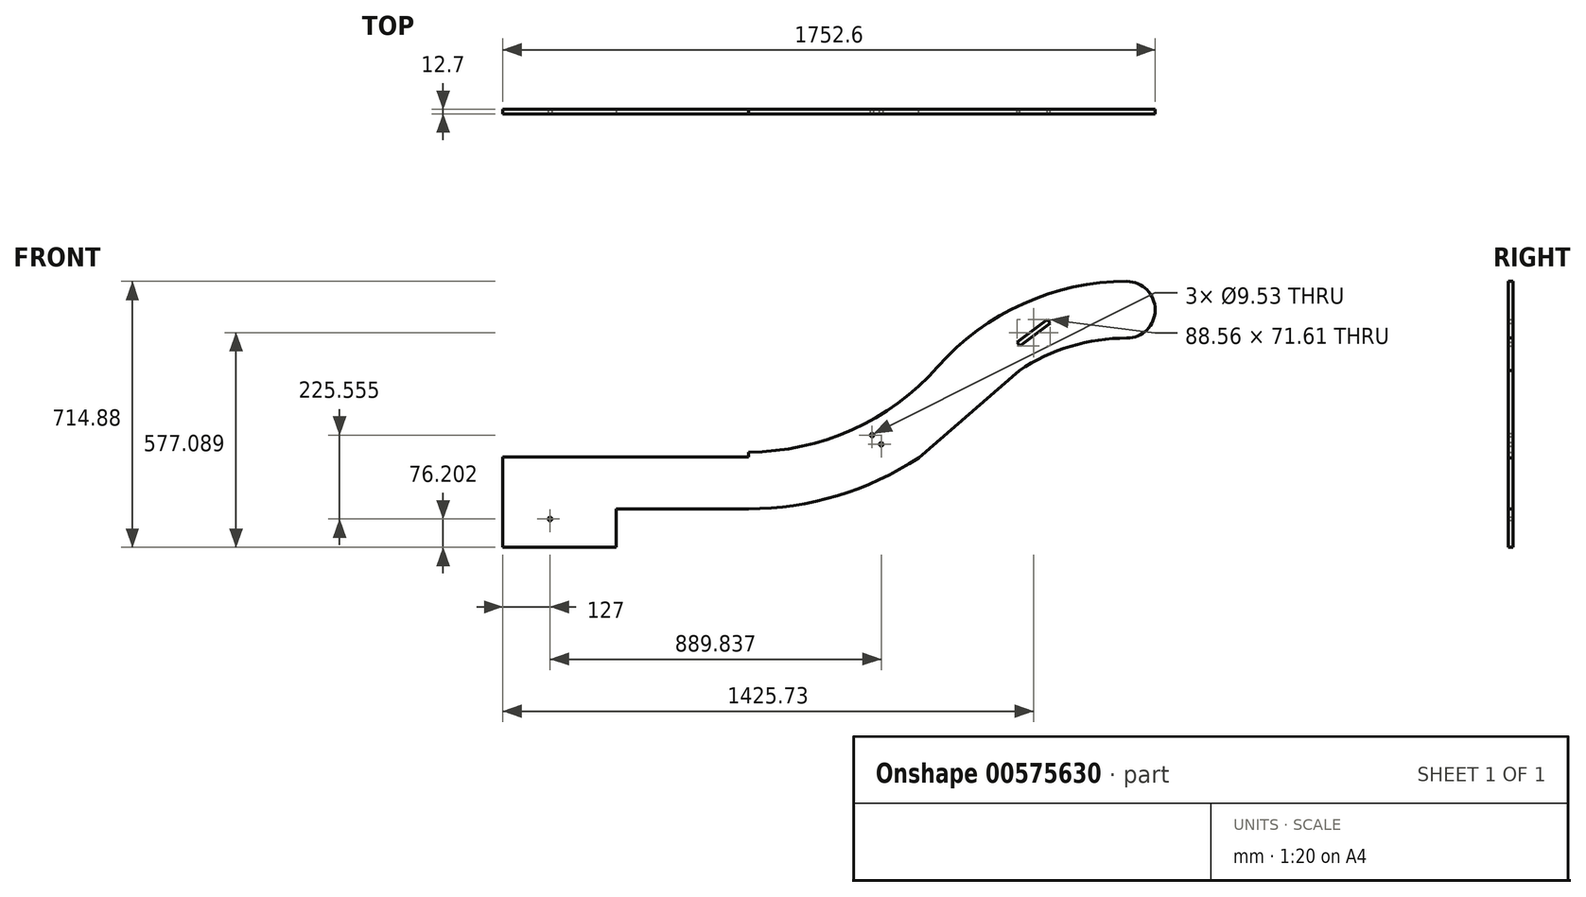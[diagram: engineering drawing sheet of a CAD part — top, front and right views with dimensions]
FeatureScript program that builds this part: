
annotation { "Feature Type Name" : "Feature", "Feature Type Description" : "" }
export const myFeature = defineFeature(function(context is Context, id is Id, definition is map)
    precondition{}
    {
        {
            var Q0;
            Q0=qCreatedBy(makeId("Front.planeOp"),FACE);
            var sketch = newSketch(context, id + "F0", { "sketchPlane" : qUnion([Q0])});
            skLineSegment(sketch, "E0", {"start": v(-1078.95, 584.06) * mm, "end": v(-570.95, 584.06) * mm, "construction": true});
            skLineSegment(sketch, "E1", {"start": v(-570.95, 584.06) * mm, "end": v(-570.95, 1042.7) * mm, "construction": true});
            skLineSegment(sketch, "E2", {"start": v(-570.95, 1042.7) * mm, "end": v(-62.95, 1042.7) * mm, "construction": true});
            skLineSegment(sketch, "E3", {"start": v(-1078.95, 57.8) * mm, "end": v(-1078.95, 584.06) * mm, "construction": true});
            skArc(sketch, "E4", {"start": v(-1078.95, 584.06) * mm, "mid": v(-800.27, 644.05) * mm, "end": v(-570.95, 813.38) * mm});
            skArc(sketch, "E5", {"start": v(-62.95, 1042.7) * mm, "mid": v(-341.63, 982.72) * mm, "end": v(-570.95, 813.38) * mm});
            skArc(sketch, "E6.0", {"start": v(-1078.95, 431.66) * mm, "mid": v(-840.53, 466.66) * mm, "end": v(-622.22, 568.68) * mm});
            skArc(sketch, "E7.0", {"start": v(-62.95, 890.3) * mm, "mid": v(-213.79, 868.16) * mm, "end": v(-351.9, 803.62) * mm});
            skLineSegment(sketch, "E8", {"start": v(-351.9, 803.62) * mm, "end": v(-622.22, 568.68) * mm});
            skLineSegment(sketch, "E9.bottom", {"start": v(-1078.95, 584.06) * mm, "end": v(-1078.95, 584.06) * mm});
            skLineSegment(sketch, "E9.top", {"start": v(-1078.95, 431.66) * mm, "end": v(-1739.35, 431.66) * mm});
            skLineSegment(sketch, "E9.left", {"start": v(-1078.95, 584.06) * mm, "end": v(-1078.95, 431.66) * mm, "construction": true});
            skLineSegment(sketch, "E9.right", {"start": v(-1739.35, 571.36) * mm, "end": v(-1739.35, 517.39) * mm});
            skArc(sketch, "E10", {"start": v(-62.95, 890.3) * mm, "mid": v(13.25, 966.5) * mm, "end": v(-62.95, 1042.7) * mm});
            skPoint(sketch, "E11.start.orphan", {"position": v(-1739.35, 507.86) * mm});
            skLineSegment(sketch, "E12.trimOffspring", {"start": v(-1739.35, 498.34) * mm, "end": v(-1739.35, 431.66) * mm});
            skArc(sketch, "E13.0", {"start": v(-62.95, 966.5) * mm, "mid": v(-193.3, 952.2) * mm, "end": v(-317.46, 909.96) * mm, "construction": true});
            skLineSegment(sketch, "E14", {"start": v(-317.46, 909.96) * mm, "end": v(-62.95, 365.37) * mm, "construction": true});
            skLineSegment(sketch, "E15", {"start": v(-62.95, 966.5) * mm, "end": v(-62.95, 365.37) * mm, "construction": true});
            skLineSegment(sketch, "E16", {"start": v(-62.95, 365.37) * mm, "end": v(-278.14, 1082.67) * mm, "construction": true});
            skPoint(sketch, "E17.start.orphan", {"position": v(-193.3, 952.2) * mm});
            skLineSegment(sketch, "E18", {"start": v(-774.15, 656.52) * mm, "end": v(-774.15, 437.24) * mm, "construction": true});
            skLineSegment(sketch, "E19", {"start": v(-774.15, 656.52) * mm, "end": v(-342.44, 224.8) * mm, "construction": true});
            skLineSegment(sketch, "E20", {"start": v(-774.15, 656.52) * mm, "end": v(-723.35, 707.31) * mm, "construction": true});
            skLineSegment(sketch, "E21.0", {"start": v(-747.2, 629.58) * mm, "end": v(-696.41, 680.37) * mm, "construction": true});
            skCircle(sketch, "E22", {"center": v(-747.2, 629.58) * mm, "radius": 4.76 * mm});
            skLineSegment(sketch, "E23.0", {"start": v(-722.51, 604.88) * mm, "end": v(-671.72, 655.68) * mm, "construction": true});
            skCircle(sketch, "E24", {"center": v(-722.51, 604.88) * mm, "radius": 4.76 * mm});
            skLineSegment(sketch, "E25", {"start": v(-1739.35, 517.39) * mm, "end": v(-1739.35, 498.34) * mm});
            skLineSegment(sketch, "E26.top", {"start": v(-1739.35, 571.36) * mm, "end": v(-1078.95, 571.36) * mm});
            skLineSegment(sketch, "E26.right", {"start": v(-1078.95, 584.06) * mm, "end": v(-1078.95, 571.36) * mm});
            skPoint(sketch, "E27.orphan", {"position": v(-1739.35, 584.06) * mm});
            skLineSegment(sketch, "E28.0", {"start": v(-350.21, 869.1) * mm, "end": v(-378.76, 847.39) * mm});
            skLineSegment(sketch, "E29.MirrorCS", {"start": v(-317.46, 909.96) * mm, "end": v(-277.03, 940.72) * mm});
            skLineSegment(sketch, "E30", {"start": v(-1739.35, 571.36) * mm, "end": v(-1739.35, 431.66) * mm});
            skLineSegment(sketch, "E31", {"start": v(-277.03, 940.72) * mm, "end": v(-269.34, 930.6) * mm});
            skLineSegment(sketch, "E32", {"start": v(-317.46, 909.96) * mm, "end": v(-357.9, 879.21) * mm});
            skLineSegment(sketch, "E33", {"start": v(-350.21, 869.1) * mm, "end": v(-357.9, 879.21) * mm});
            skLineSegment(sketch, "E34", {"start": v(-378.76, 847.39) * mm, "end": v(-269.34, 930.6) * mm});
            skLineSegment(sketch, "E35", {"start": v(-241.17, 948.18) * mm, "end": v(-233.48, 938.07) * mm});
            skLineSegment(sketch, "E36.1.0", {"start": v(-408.17, 857.5) * mm, "end": v(-62.95, 365.37) * mm, "construction": true});
            skLineSegment(sketch, "E36.anchor1", {"start": v(-62.95, 365.37) * mm, "end": v(-317.46, 909.96) * mm, "construction": true});
            skLineSegment(sketch, "E36.anchor2", {"start": v(-62.95, 365.37) * mm, "end": v(-488.38, 790.07) * mm, "construction": true});
            skLineSegment(sketch, "E37.0", {"start": v(-774.15, 584.06) * mm, "end": v(-774.15, 431.66) * mm, "construction": true});
            skLineSegment(sketch, "E38", {"start": v(-774.15, 584.06) * mm, "end": v(-774.15, 656.52) * mm, "construction": true});
            skSolve(sketch);
        }
        {
            var Q0;
            Q0=qSketchRegion(id+"F0",true);
            extrude(context, id + "F1", {"entities" : qUnion([Q0]), "depth" : 12.7 * mm, "offsetDistance" : 25.4 * mm});
        }
        {
            var Q0;
            Q0=makeQuery(id+"F1.opExtrude","CAP_FACE",FACE,{"disambiguationData":[OSD([sQuery(id+"F0.wireOp",EDGE,"E4"),sQuery(id+"F0.wireOp",EDGE,"E5"),sQuery(id+"F0.wireOp",EDGE,"E6.0"),sQuery(id+"F0.wireOp",EDGE,"E7.0"),sQuery(id+"F0.wireOp",EDGE,"E8"),sQuery(id+"F0.wireOp",EDGE,"E9.bottom"),sQuery(id+"F0.wireOp",EDGE,"E9.top"),sQuery(id+"F0.wireOp",EDGE,"E10"),sQuery(id+"F0.wireOp",EDGE,"E22"),sQuery(id+"F0.wireOp",EDGE,"E24"),sQuery(id+"F0.wireOp",EDGE,"E26.top"),sQuery(id+"F0.wireOp",EDGE,"E26.right"),sQuery(id+"F0.wireOp",EDGE,"rGuNlkWs-DwgR-RLvr-mMdR-KLj3d7VYUrrU"),sQuery(id+"F0.wireOp",EDGE,"E28.0"),sQuery(id+"F0.wireOp",EDGE,"E29.MirrorCS"),sQuery(id+"F0.wireOp",EDGE,"bdf513aa-e08c-4932-959c-efffc82560380.MirrorCS"),sQuery(id+"F0.wireOp",EDGE,"18Rq9EtM-grnE-uFA9-u4ZY-gGSRGGMkSvjP"),sQuery(id+"F0.wireOp",EDGE,"AyWyaUEp-hzy5-DDg5-a3wd-rfjwWbH5fqIC"),sQuery(id+"F0.wireOp",EDGE,"E30")])],"isStart":false});
            var sketch = newSketch(context, id + "F2", { "sketchPlane" : qUnion([Q0])});
            skLineSegment(sketch, "E39", {"start": v(-317.46, 909.96) * mm, "end": v(-9.94, 505.62) * mm, "construction": true});
            skCircle(sketch, "E40", {"center": v(-9.94, 505.62) * mm, "radius": 254 * mm, "construction": true});
            skLineSegment(sketch, "E41", {"start": v(-9.94, 251.62) * mm, "end": v(-1739.35, 251.62) * mm, "construction": true});
            skLineSegment(sketch, "E42.top", {"start": v(-1739.35, 431.66) * mm, "end": v(-1741.67, 431.66) * mm});
            skLineSegment(sketch, "E43", {"start": v(-1739.35, 251.62) * mm, "end": v(-1739.35, 431.66) * mm});
            skLineSegment(sketch, "E44.0", {"start": v(-1612.35, -106.65) * mm, "end": v(-1612.35, 431.66) * mm, "construction": true});
            skCircle(sketch, "E45", {"center": v(-1612.35, 404.02) * mm, "radius": 4.76 * mm});
            skLineSegment(sketch, "E46.left", {"start": v(-1739.35, 45.75) * mm, "end": v(-1739.35, -30.45) * mm});
            skLineSegment(sketch, "E47.0", {"start": v(-1434.55, 327.82) * mm, "end": v(-1434.55, 431.66) * mm});
            skLineSegment(sketch, "E48.trimOffspring", {"start": v(-1434.55, 327.82) * mm, "end": v(-1739.35, 327.82) * mm});
            skLineSegment(sketch, "E49.trimOffspring", {"start": v(-1434.55, 404.02) * mm, "end": v(-1603.53, 404.02) * mm, "construction": true});
            skLineSegment(sketch, "E50", {"start": v(-1739.35, 431.66) * mm, "end": v(-1434.55, 431.66) * mm});
            skSolve(sketch);
        }
        {
            var Q0;
            Q0=qSketchRegion(id+"F2",true);
            extrude(context, id + "F3", {"entities" : qUnion([Q0]), "operationType" : NewBodyOperationType.ADD, "oppositeDirection" : true, "depth" : 12.7 * mm, "offsetDistance" : 25.4 * mm});
        }
    });
